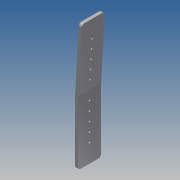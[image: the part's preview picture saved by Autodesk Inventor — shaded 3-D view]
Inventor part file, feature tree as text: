
AUTODESK INVENTOR PART (.ipt)
format: ipt  version: 2014 SP1 (Build 180222100, 222)  size: 137,216 bytes
history: native  units: in
note: dims shown in document units (in); Inventor stores cm internally (conversion verified against a paired STEP export)
features: sketch x5, hole x3, extrude x1, sheet_metal_op x1
ambient origin geometry x8: Origin, YZ Plane, XZ Plane, XY Plane, X Axis, Y Axis, Z Axis, Center Point
bodies: Solid1 (feature_tree)
feature tree (10):
  extrude  "Extrusion1"  Depth=1.0in
  hole  "Hole2"  [1 undecoded]
  sheet_metal_op  "Fold1"
  hole  "Hole3"  [1 undecoded]
  hole  "Hole4"  [1 undecoded]
  sketch  "Sketch1"  dims[d0=1.0in d1=5.5118in]
  sketch  "Sketch3"  dims[d2=0.125in d3=0.12in d4=0.0in]
  sketch  "Sketch4"  dims[d29=0.7874in d30=2.3622in d32=0.7874in d33=0.3937in d35=1.0in]
  sketch  "Sketch5"  dims[d37=0.0787in d38=0.75in d39=0.375in d40=0.25in d41=0.5635in d42=1.0in d43=0.8108in d44=0.12in]
  sketch  "Sketch6"  dims[d45=0.06in d46=0.24in d47=0.12in d48=0.0227in d49=0.12in d50=0.3937in d51=0.7874in d53=0.7874in d54=0.3937in d56=1.0in d58=0.0787in d59=0.75in d60=0.375in d61=0.25in d62=0.5635in d63=0.12in d64=0.8108in d65=0.3937in d66=0.7874in d68=0.7874in d69=0.3937in d71=1.0in d73=0.0787in d74=0.75in d75=0.375in d76=0.25in d77=0.5635in d78=0.12in d79=0.8108in]
note: 3 required parameter values undecoded (feature->parameter linkage not recoverable at this tier; creation-order binding heuristic only, values carry confidence <= 0.55)
